FCSTD DOCUMENT  (FreeCAD 0.17R13541 (Git))
Label: footprints
License: All rights reserved
LicenseURL: http://en.wikipedia.org/wiki/All_rights_reserved
objects: Sketcher::SketchObject×2, Part::Part2DObjectPython×2
note: 4 computed .brp shape members not serialized (recipe doc carries the construction recipe); baked Part::Feature solids carry a one-line shape summary decoded from their .brp

FEATURE [Sketcher::SketchObject] Sketch002  label="HAHN Trafo Footprint"
  sketch-geometry (14):
    g0: LineSegment StartX=0 StartY=0 StartZ=0 EndX=20 EndY=0 EndZ=0
    g1: LineSegment StartX=20 StartY=0 StartZ=0 EndX=20 EndY=-45 EndZ=0
    g2: LineSegment StartX=20 StartY=-45 StartZ=0 EndX=0 EndY=-45 EndZ=0
    g3: LineSegment StartX=0 StartY=-45 StartZ=0 EndX=0 EndY=0 EndZ=0
    g4: LineSegment StartX=26 StartY=0 StartZ=0 EndX=46 EndY=0 EndZ=0
    g5: LineSegment StartX=46 StartY=0 StartZ=0 EndX=46 EndY=-45 EndZ=0
    g6: LineSegment StartX=46 StartY=-45 StartZ=0 EndX=26 EndY=-45 EndZ=0
    g7: LineSegment StartX=26 StartY=-45 StartZ=0 EndX=26 EndY=0 EndZ=0
    g8: LineSegment StartX=-5.85 StartY=11.8 StartZ=0 EndX=51.85 EndY=11.8 EndZ=0
    g9: LineSegment StartX=51.85 StartY=11.8 StartZ=0 EndX=51.85 EndY=-56.8 EndZ=0
    g10: LineSegment StartX=51.85 StartY=-56.8 StartZ=0 EndX=-5.85 EndY=-56.8 EndZ=0
    g11: LineSegment StartX=-5.85 StartY=-56.8 StartZ=0 EndX=-5.85 EndY=11.8 EndZ=0
    g12: LineSegment [constr] StartX=-5.85 StartY=-22.5 StartZ=0 EndX=51.85 EndY=-22.5 EndZ=0
    g13: LineSegment [constr] StartX=23 StartY=11.8 StartZ=0 EndX=23 EndY=-56.8 EndZ=0
  constraints (42):
    c: Coincident(g0,g1)
    c: Coincident(g1,g2)
    c: Coincident(g2,g3)
    c: Coincident(g3,g0)
    c: Horizontal(g0)
    c: Horizontal(g2)
    c: Vertical(g1)
    c: Vertical(g3)
    c: DistanceX(g0,g0) = 20
    c: DistanceY(g3,g3) = 45
    c: Coincident(g4,g5)
    c: Coincident(g5,g6)
    c: Coincident(g6,g7)
    c: Coincident(g7,g4)
    c: Horizontal(g4)
    c: Horizontal(g6)
    c: Vertical(g5)
    c: Vertical(g7)
    c: DistanceY(g7,g7) = 45
    c: DistanceX(g4,g4) = 20
    c: Coincident(g0,g-1)
    c: PointOnObject(g4,g-1)
    c: DistanceX(g0,g4) = 6
    c: Coincident(g8,g9)
    c: Coincident(g9,g10)
    c: Coincident(g10,g11)
    c: Coincident(g11,g8)
    c: Horizontal(g8)
    c: Horizontal(g10)
    c: Vertical(g9)
    c: Vertical(g11)
    c: DistanceX(g8,g8) = 57.7
    c: DistanceY(g11,g11) = 68.6
    c: Vertical(g13)
    c: Symmetric(g8,g8,g13)
    c: Symmetric(g0,g4,g13)
    c: Symmetric(g9,g8,g12)
    c: Symmetric(g4,g5,g12)
    c: PointOnObject(g12,g9)
    c: PointOnObject(g12,g11)
    c: PointOnObject(g13,g8)
    c: PointOnObject(g13,g10)
FEATURE [Part::Part2DObjectPython] Shape2DView001  label="HAHN Trafo Footprint Shape"  # Draft 2D object (typed FeaturePython)
  Base = -> Sketch002
  HiddenLines = false
  InPlace = true
  Projection = (0,0,1)
  ProjectionMode = 0
  SegmentLength = 0.05
  Tessellation = false
  VisibleOnly = false
FEATURE [Sketcher::SketchObject] Sketch003  label="Myrra UI 39 Trafo Footprint"
  expr: Constraints[40] = 1
  expr: Constraints[17] = 2.5 / 2
  sketch-geometry (15):
    g0: LineSegment StartX=-5.5 StartY=11.5 StartZ=0 EndX=51.5 EndY=11.5 EndZ=0
    g1: LineSegment StartX=51.5 StartY=11.5 StartZ=0 EndX=51.5 EndY=-56.5 EndZ=0
    g2: LineSegment StartX=51.5 StartY=-56.5 StartZ=0 EndX=-5.5 EndY=-56.5 EndZ=0
    g3: LineSegment StartX=-5.5 StartY=-56.5 StartZ=0 EndX=-5.5 EndY=11.5 EndZ=0
    g4: Circle CenterX=48 CenterY=8.75 CenterZ=0 NormalX=0 NormalY=0 NormalZ=1 AngleXU=0 Radius=1.25
    g5: Circle CenterX=-2 CenterY=8.75 CenterZ=0 NormalX=0 NormalY=0 NormalZ=1 AngleXU=0 Radius=1.25
    g6: Circle CenterX=-2 CenterY=-53.75 CenterZ=0 NormalX=0 NormalY=0 NormalZ=1 AngleXU=0 Radius=1.25
    g7: Circle CenterX=48 CenterY=-53.75 CenterZ=0 NormalX=0 NormalY=0 NormalZ=1 AngleXU=0 Radius=1.25
    g8: LineSegment [constr] StartX=23 StartY=11.5 StartZ=0 EndX=23 EndY=-56.5 EndZ=0
    g9: LineSegment [constr] StartX=-5.5 StartY=-22.5 StartZ=0 EndX=51.5 EndY=-22.5 EndZ=0
    g10: LineSegment [constr] StartX=0 StartY=0 StartZ=0 EndX=46 EndY=0 EndZ=0
    g11: LineSegment [constr] StartX=46 StartY=0 StartZ=0 EndX=46 EndY=-45 EndZ=0
    g12: LineSegment [constr] StartX=46 StartY=-45 StartZ=0 EndX=0 EndY=-45 EndZ=0
    g13: LineSegment [constr] StartX=0 StartY=-45 StartZ=0 EndX=0 EndY=0 EndZ=0
    g14: Circle CenterX=0 CenterY=0 CenterZ=0 NormalX=0 NormalY=0 NormalZ=1 AngleXU=0 Radius=1
  constraints (41):
    c: Coincident(g0,g1)
    c: Coincident(g1,g2)
    c: Coincident(g2,g3)
    c: Coincident(g3,g0)
    c: Horizontal(g0)
    c: Horizontal(g2)
    c: Vertical(g1)
    c: Vertical(g3)
    c: DistanceX(g0,g0) = 57
    c: DistanceY(g1,g1) = 68
    c: PointOnObject(g8,g0)
    c: PointOnObject(g8,g2)
    c: PointOnObject(g9,g3)
    c: PointOnObject(g9,g1)
    c: Horizontal(g9)
    c: Symmetric(g0,g0,g8)
    c: Symmetric(g0,g2,g9)
    c: Radius(g5) = 1.25
    c: Equal(g5,g4)
    c: Equal(g5,g7)
    c: Equal(g5,g6)
    c: Symmetric(g5,g4,g8)
    c: Symmetric(g6,g7,g8)
    c: Symmetric(g5,g6,g9)
    c: DistanceY(g6,g5) = 62.5
    c: DistanceX(g5,g4) = 50
    c: Coincident(g10,g11)
    c: Coincident(g11,g12)
    c: Coincident(g12,g13)
    c: Coincident(g13,g10)
    c: Horizontal(g10)
    c: Horizontal(g12)
    c: Vertical(g11)
    c: Vertical(g13)
    c: DistanceY(g13,g13) = 45
    c: DistanceX(g10,g10) = 46
    c: Symmetric(g10,g10,g8)
    c: Symmetric(g10,g12,g9)
    c: Coincident(g10,g-1)
    c: Coincident(g14,g-1)
    c: Radius(g14) = 1
FEATURE [Part::Part2DObjectPython] Shape2DView002  label="Myrra UI 39 Trafo Footprint Shape"  # Draft 2D object (typed FeaturePython)
  Base = -> Sketch003
  HiddenLines = false
  InPlace = true
  Projection = (0,0,1)
  ProjectionMode = 0
  SegmentLength = 0.05
  Tessellation = false
  VisibleOnly = false
